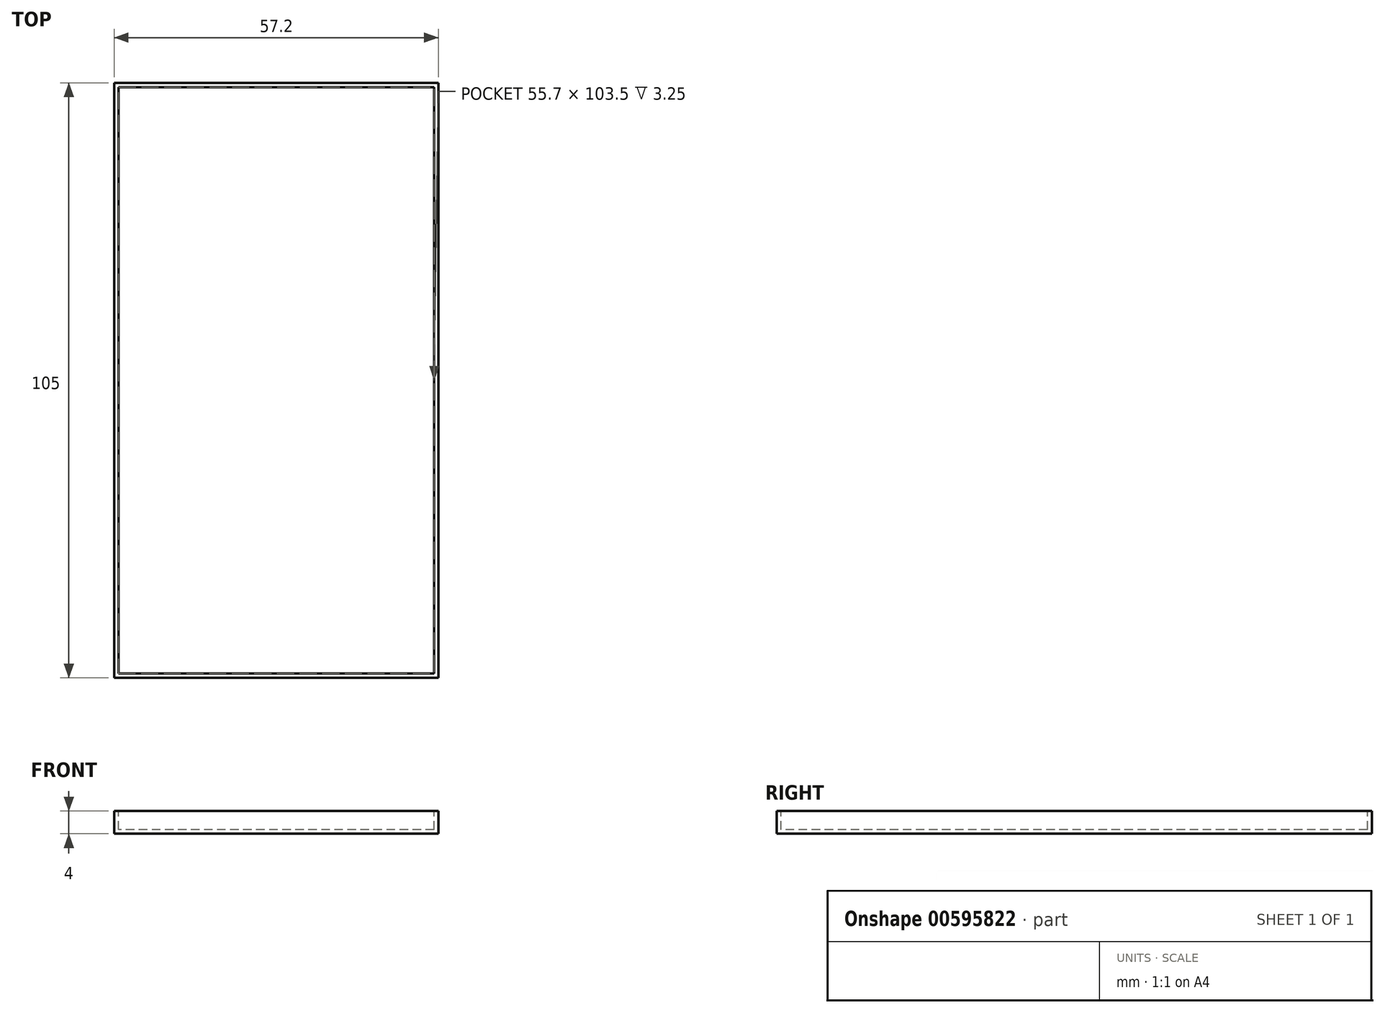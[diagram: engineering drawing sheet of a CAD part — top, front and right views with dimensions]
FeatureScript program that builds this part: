
annotation { "Feature Type Name" : "Feature", "Feature Type Description" : "" }
export const myFeature = defineFeature(function(context is Context, id is Id, definition is map)
    precondition{}
    {
        {
            var Q0;
            Q0=qCreatedBy(makeId("Top.planeOp"),FACE);
            var sketch = newSketch(context, id + "F0", { "sketchPlane" : qUnion([Q0])});
            skLineSegment(sketch, "E0.bottom", {"start": v(-57.2, 50.17) * mm, "end": v(0, 50.17) * mm});
            skLineSegment(sketch, "E0.top", {"start": v(-57.2, -54.83) * mm, "end": v(0, -54.83) * mm});
            skLineSegment(sketch, "E0.left", {"start": v(-57.2, 50.17) * mm, "end": v(-57.2, -54.83) * mm});
            skLineSegment(sketch, "E0.right", {"start": v(0, 50.17) * mm, "end": v(0, -54.83) * mm});
            skSolve(sketch);
        }
        {
            var Q0;
            Q0=makeQuery(id+"F0.imprint","IMPRINT",FACE,{"disambiguationData":[TD([[makeQuery(id+"F0.imprint","IMPRINT",EDGE,{"derivedFrom":sQuery(id+"F0.wireOp",EDGE,"E0.bottom")}),-1.0]])]});
            var Q1;
            Q1=qSketchRegion(id+"F0",true);
            extrude(context, id + "F1", {"entities" : qUnion([Q0, Q1]), "depth" : 4 * mm, "offsetDistance" : 25.4 * mm});
        }
        {
            var Q0;
            Q0=makeQuery(id+"F1.opExtrude","CAP_FACE",FACE,{"disambiguationData":[OSD([sQuery(id+"F0.wireOp",EDGE,"E0.bottom"),sQuery(id+"F0.wireOp",EDGE,"E0.top"),sQuery(id+"F0.wireOp",EDGE,"E0.left"),sQuery(id+"F0.wireOp",EDGE,"E0.right")])],"isStart":false});
            var sketch = newSketch(context, id + "F2", { "sketchPlane" : qUnion([Q0])});
            skLineSegment(sketch, "E1.bottom", {"start": v(-0.75, 49.42) * mm, "end": v(-56.45, 49.42) * mm});
            skLineSegment(sketch, "E1.top", {"start": v(-0.75, -54.08) * mm, "end": v(-56.45, -54.08) * mm});
            skLineSegment(sketch, "E1.left", {"start": v(-0.75, 49.42) * mm, "end": v(-0.75, -54.08) * mm});
            skLineSegment(sketch, "E1.right", {"start": v(-56.45, 49.42) * mm, "end": v(-56.45, -54.08) * mm});
            skPoint(sketch, "E1.middle", {"position": v(-28.6, -2.33) * mm});
            skSolve(sketch);
        }
        {
            var Q0;
            Q0=makeQuery(id+"F2.imprint","IMPRINT",FACE,{"disambiguationData":[TD([[makeQuery(id+"F2.imprint","IMPRINT",EDGE,{"derivedFrom":sQuery(id+"F2.wireOp",EDGE,"E1.bottom")}),1.0]])]});
            extrude(context, id + "F3", {"entities" : qUnion([Q0]), "operationType" : NewBodyOperationType.REMOVE, "oppositeDirection" : true, "depth" : 3.25 * mm, "offsetDistance" : 25.4 * mm});
        }
    });
